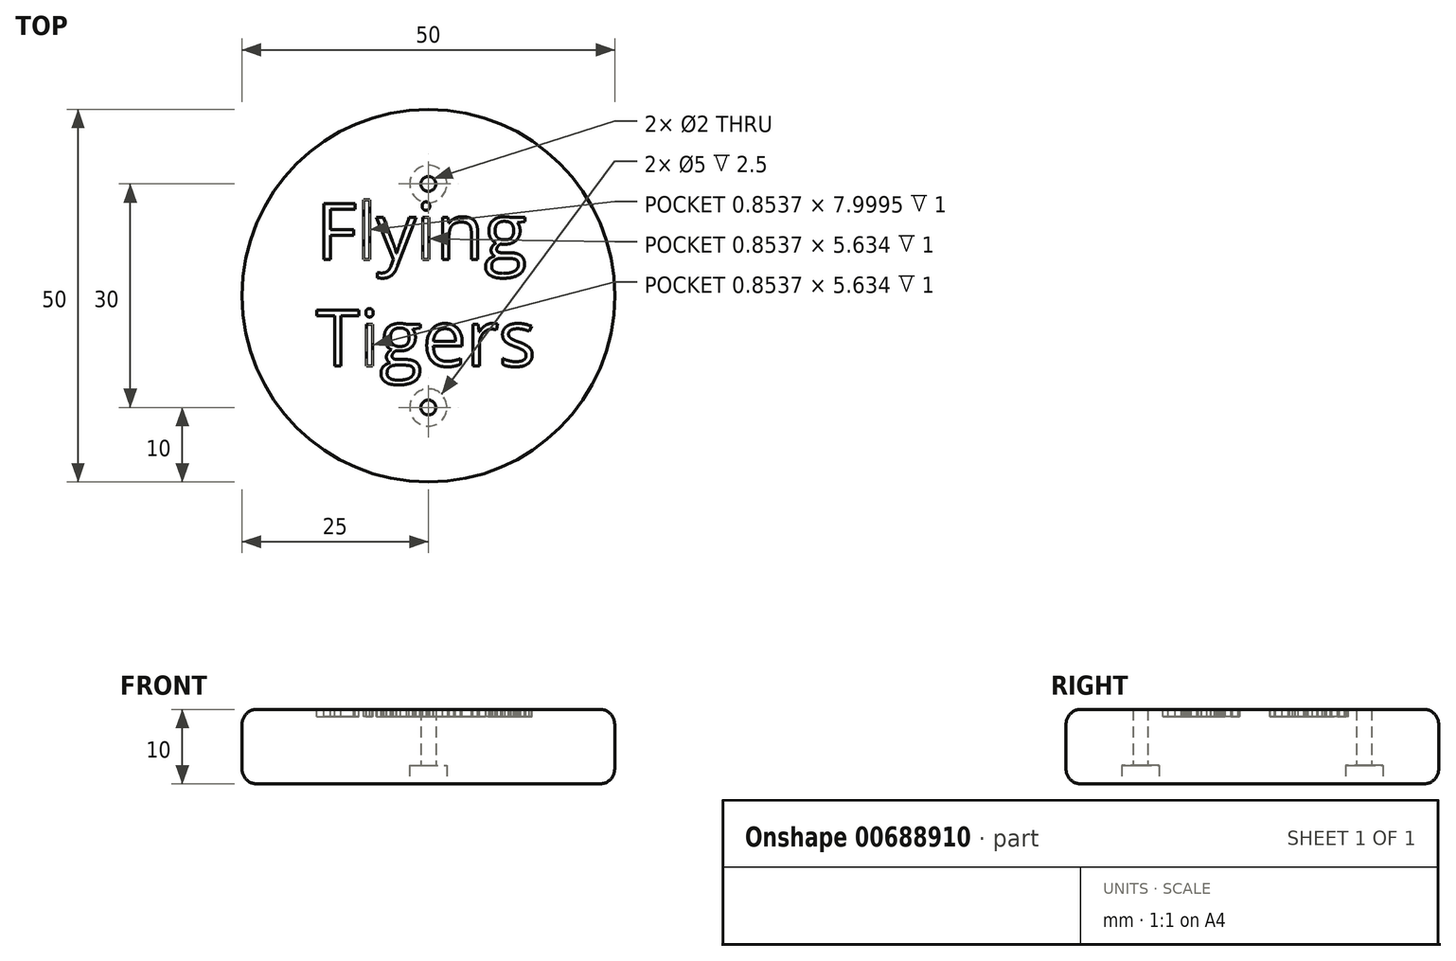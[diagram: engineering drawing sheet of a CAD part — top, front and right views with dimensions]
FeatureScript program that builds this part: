
annotation { "Feature Type Name" : "Feature", "Feature Type Description" : "" }
export const myFeature = defineFeature(function(context is Context, id is Id, definition is map)
    precondition{}
    {
        {
            var Q0;
            Q0=qCreatedBy(makeId("Top.planeOp"),FACE);
            var sketch = newSketch(context, id + "F0", { "sketchPlane" : qUnion([Q0])});
            skCircle(sketch, "E0", {"center": v(0, 0) * mm, "radius": 25 * mm});
            skSolve(sketch);
        }
        {
            var Q0;
            Q0=qSketchRegion(id+"F0",true);
            extrude(context, id + "F1", {"entities" : qUnion([Q0]), "depth" : 10 * mm});
        }
        {
            var Q0;
            Q0=makeQuery(id+"F1.opExtrude","CAP_FACE",FACE,{"disambiguationData":[OSD([sQuery(id+"F0.wireOp",EDGE,"E0")])],"isStart":false});
            var sketch = newSketch(context, id + "F2", { "sketchPlane" : qUnion([Q0])});
            skText(sketch, "E1", { "text": "GO DOGS", "fontName": "OpenSans-Bold.ttf"});
            const initialGuessF2  = {"E1": [-0.02326, -0.00364, 1, 0, 0.007]};
            skSetInitialGuess(sketch, initialGuessF2);
            skSolve(sketch);
        }
        {
            var Q0;
            Q0=qSketchRegion(id+"F2",true);
            extrude(context, id + "F3", {"entities" : qUnion([Q0]), "operationType" : NewBodyOperationType.REMOVE, "oppositeDirection" : true, "depth" : 1 * mm});
        }
        {
            var Q0;
            Q0=makeQuery(id+"F1.opExtrude","CAP_EDGE",EDGE,{"disambiguationData":[OSD([sQuery(id+"F0.wireOp",EDGE,"E0")])],"isStart":false});
            var Q1;
            Q1=makeQuery(id+"F1.opExtrude","CAP_EDGE",EDGE,{"disambiguationData":[OSD([sQuery(id+"F0.wireOp",EDGE,"E0")])],"isStart":true});
            fillet(context, id + "F4", {"entities" : qUnion([Q0, Q1]), "radius" : 2 * mm, "tangentPropagation" : true, "allowEdgeOverflow" : false});
        }
        {
            var Q0;
            Q0=makeQuery(id+"F1.opExtrude","CAP_FACE",FACE,{"disambiguationData":[OSD([sQuery(id+"F0.wireOp",EDGE,"E0")])],"isStart":true});
            var sketch = newSketch(context, id + "F5", { "sketchPlane" : qUnion([Q0])});
            skPoint(sketch, "E2", {"position": v(0, 15) * mm});
            skPoint(sketch, "E3", {"position": v(0, -15) * mm});
            skSolve(sketch);
        }
        {
            var Q0;
            Q0=sQuery(id+"F5.wireOp",VERTEX,"E2");
            var Q1;
            Q1=sQuery(id+"F5.wireOp",VERTEX,"E3");
            var Q2;
            Q2=makeQuery(id+"F1.opExtrude","SWEPT_BODY",BODY,{"disambiguationData":[OSD([sQuery(id+"F0.wireOp",EDGE,"E0")])]});
            hole(context, id + "F6", {"style" : HoleStyle.C_BORE, "endStyle" : HoleEndStyle.THROUGH, "holeDiameter" : 2 * mm, "cBoreDiameter" : 5 * mm, "cBoreDepth" : 2.5 * mm, "startFromSketch" : true, "locations" : qUnion([Q0, Q1]), "scope" : qUnion([Q2]), "isTappedThrough" : true});
        }
        {
            var Q0;
            Q0=makeQuery(id+"F3.boolean.opBoolean","COPY",FACE,{"derivedFrom":makeQuery(id+"F3.opExtrude","CAP_FACE",FACE,{"disambiguationData":[OSD([sQuery(id+"F2.wireOp",EDGE,"E1.sketch_text.stroke-0"),sQuery(id+"F2.wireOp",EDGE,"E1.sketch_text.stroke-1"),sQuery(id+"F2.wireOp",EDGE,"E1.sketch_text.stroke-2"),sQuery(id+"F2.wireOp",EDGE,"E1.sketch_text.stroke-3"),sQuery(id+"F2.wireOp",EDGE,"E1.sketch_text.stroke-4"),sQuery(id+"F2.wireOp",EDGE,"E1.sketch_text.stroke-5"),sQuery(id+"F2.wireOp",EDGE,"E1.sketch_text.stroke-6"),sQuery(id+"F2.wireOp",EDGE,"E1.sketch_text.stroke-7"),sQuery(id+"F2.wireOp",EDGE,"E1.sketch_text.stroke-8"),sQuery(id+"F2.wireOp",EDGE,"E1.sketch_text.stroke-9"),sQuery(id+"F2.wireOp",EDGE,"E1.sketch_text.stroke-10"),sQuery(id+"F2.wireOp",EDGE,"E1.sketch_text.stroke-11"),sQuery(id+"F2.wireOp",EDGE,"E1.sketch_text.stroke-12"),sQuery(id+"F2.wireOp",EDGE,"E1.sketch_text.stroke-13"),sQuery(id+"F2.wireOp",EDGE,"E1.sketch_text.stroke-14"),sQuery(id+"F2.wireOp",EDGE,"E1.sketch_text.stroke-15"),sQuery(id+"F2.wireOp",EDGE,"E1.sketch_text.stroke-16"),sQuery(id+"F2.wireOp",EDGE,"E1.sketch_text.stroke-17"),sQuery(id+"F2.wireOp",EDGE,"E1.sketch_text.stroke-18")])],"isStart":false})});
            extrude(context, id + "F7", {"entities" : qUnion([Q0]), "operationType" : NewBodyOperationType.ADD, "depth" : 1 * mm, "offsetDistance" : 25 * mm});
        }
        {
            var Q0;
            Q0=makeQuery(id+"F3.boolean.opBoolean","COPY",FACE,{"derivedFrom":makeQuery(id+"F3.opExtrude","CAP_FACE",FACE,{"disambiguationData":[OSD([sQuery(id+"F2.wireOp",EDGE,"E1.sketch_text.stroke-19"),sQuery(id+"F2.wireOp",EDGE,"E1.sketch_text.stroke-20"),sQuery(id+"F2.wireOp",EDGE,"E1.sketch_text.stroke-21"),sQuery(id+"F2.wireOp",EDGE,"E1.sketch_text.stroke-22"),sQuery(id+"F2.wireOp",EDGE,"E1.sketch_text.stroke-23"),sQuery(id+"F2.wireOp",EDGE,"E1.sketch_text.stroke-24"),sQuery(id+"F2.wireOp",EDGE,"E1.sketch_text.stroke-25"),sQuery(id+"F2.wireOp",EDGE,"E1.sketch_text.stroke-26"),sQuery(id+"F2.wireOp",EDGE,"E1.sketch_text.stroke-27"),sQuery(id+"F2.wireOp",EDGE,"E1.sketch_text.stroke-28"),sQuery(id+"F2.wireOp",EDGE,"E1.sketch_text.stroke-29"),sQuery(id+"F2.wireOp",EDGE,"E1.sketch_text.stroke-30"),sQuery(id+"F2.wireOp",EDGE,"E1.sketch_text.stroke-31"),sQuery(id+"F2.wireOp",EDGE,"E1.sketch_text.stroke-32")])],"isStart":false})});
            extrude(context, id + "F8", {"entities" : qUnion([Q0]), "operationType" : NewBodyOperationType.ADD, "depth" : 1 * mm, "offsetDistance" : 25 * mm});
        }
        {
            var Q0;
            Q0=makeQuery(id+"F3.boolean.opBoolean","COPY",FACE,{"derivedFrom":makeQuery(id+"F3.opExtrude","CAP_FACE",FACE,{"disambiguationData":[OSD([sQuery(id+"F2.wireOp",EDGE,"E1.sketch_text.stroke-33"),sQuery(id+"F2.wireOp",EDGE,"E1.sketch_text.stroke-34"),sQuery(id+"F2.wireOp",EDGE,"E1.sketch_text.stroke-35"),sQuery(id+"F2.wireOp",EDGE,"E1.sketch_text.stroke-36"),sQuery(id+"F2.wireOp",EDGE,"E1.sketch_text.stroke-37"),sQuery(id+"F2.wireOp",EDGE,"E1.sketch_text.stroke-38"),sQuery(id+"F2.wireOp",EDGE,"E1.sketch_text.stroke-39"),sQuery(id+"F2.wireOp",EDGE,"E1.sketch_text.stroke-40"),sQuery(id+"F2.wireOp",EDGE,"E1.sketch_text.stroke-41"),sQuery(id+"F2.wireOp",EDGE,"E1.sketch_text.stroke-42"),sQuery(id+"F2.wireOp",EDGE,"E1.sketch_text.stroke-43"),sQuery(id+"F2.wireOp",EDGE,"E1.sketch_text.stroke-44")])],"isStart":false})});
            extrude(context, id + "F9", {"entities" : qUnion([Q0]), "operationType" : NewBodyOperationType.ADD, "depth" : 1 * mm, "offsetDistance" : 25 * mm});
        }
        {
            var Q0;
            Q0=makeQuery(id+"F3.boolean.opBoolean","COPY",FACE,{"derivedFrom":makeQuery(id+"F3.opExtrude","CAP_FACE",FACE,{"disambiguationData":[OSD([sQuery(id+"F2.wireOp",EDGE,"E1.sketch_text.stroke-59"),sQuery(id+"F2.wireOp",EDGE,"E1.sketch_text.stroke-60"),sQuery(id+"F2.wireOp",EDGE,"E1.sketch_text.stroke-61"),sQuery(id+"F2.wireOp",EDGE,"E1.sketch_text.stroke-62"),sQuery(id+"F2.wireOp",EDGE,"E1.sketch_text.stroke-63"),sQuery(id+"F2.wireOp",EDGE,"E1.sketch_text.stroke-64"),sQuery(id+"F2.wireOp",EDGE,"E1.sketch_text.stroke-65"),sQuery(id+"F2.wireOp",EDGE,"E1.sketch_text.stroke-66"),sQuery(id+"F2.wireOp",EDGE,"E1.sketch_text.stroke-67"),sQuery(id+"F2.wireOp",EDGE,"E1.sketch_text.stroke-68"),sQuery(id+"F2.wireOp",EDGE,"E1.sketch_text.stroke-69"),sQuery(id+"F2.wireOp",EDGE,"E1.sketch_text.stroke-70"),sQuery(id+"F2.wireOp",EDGE,"E1.sketch_text.stroke-71"),sQuery(id+"F2.wireOp",EDGE,"E1.sketch_text.stroke-72"),sQuery(id+"F2.wireOp",EDGE,"E1.sketch_text.stroke-73"),sQuery(id+"F2.wireOp",EDGE,"E1.sketch_text.stroke-74"),sQuery(id+"F2.wireOp",EDGE,"E1.sketch_text.stroke-75"),sQuery(id+"F2.wireOp",EDGE,"E1.sketch_text.stroke-76"),sQuery(id+"F2.wireOp",EDGE,"E1.sketch_text.stroke-77")])],"isStart":false})});
            var Q1;
            Q1=makeQuery(id+"F3.boolean.opBoolean","COPY",FACE,{"derivedFrom":makeQuery(id+"F3.opExtrude","CAP_FACE",FACE,{"disambiguationData":[OSD([sQuery(id+"F2.wireOp",EDGE,"E1.sketch_text.stroke-45"),sQuery(id+"F2.wireOp",EDGE,"E1.sketch_text.stroke-46"),sQuery(id+"F2.wireOp",EDGE,"E1.sketch_text.stroke-47"),sQuery(id+"F2.wireOp",EDGE,"E1.sketch_text.stroke-48"),sQuery(id+"F2.wireOp",EDGE,"E1.sketch_text.stroke-49"),sQuery(id+"F2.wireOp",EDGE,"E1.sketch_text.stroke-50"),sQuery(id+"F2.wireOp",EDGE,"E1.sketch_text.stroke-51"),sQuery(id+"F2.wireOp",EDGE,"E1.sketch_text.stroke-52"),sQuery(id+"F2.wireOp",EDGE,"E1.sketch_text.stroke-53"),sQuery(id+"F2.wireOp",EDGE,"E1.sketch_text.stroke-54"),sQuery(id+"F2.wireOp",EDGE,"E1.sketch_text.stroke-55"),sQuery(id+"F2.wireOp",EDGE,"E1.sketch_text.stroke-56"),sQuery(id+"F2.wireOp",EDGE,"E1.sketch_text.stroke-57"),sQuery(id+"F2.wireOp",EDGE,"E1.sketch_text.stroke-58")])],"isStart":false})});
            var Q2;
            Q2=makeQuery(id+"F3.boolean.opBoolean","COPY",FACE,{"derivedFrom":makeQuery(id+"F3.opExtrude","CAP_FACE",FACE,{"disambiguationData":[OSD([sQuery(id+"F2.wireOp",EDGE,"E1.sketch_text.stroke-78"),sQuery(id+"F2.wireOp",EDGE,"E1.sketch_text.stroke-79"),sQuery(id+"F2.wireOp",EDGE,"E1.sketch_text.stroke-80"),sQuery(id+"F2.wireOp",EDGE,"E1.sketch_text.stroke-81"),sQuery(id+"F2.wireOp",EDGE,"E1.sketch_text.stroke-82"),sQuery(id+"F2.wireOp",EDGE,"E1.sketch_text.stroke-83"),sQuery(id+"F2.wireOp",EDGE,"E1.sketch_text.stroke-84"),sQuery(id+"F2.wireOp",EDGE,"E1.sketch_text.stroke-85"),sQuery(id+"F2.wireOp",EDGE,"E1.sketch_text.stroke-86"),sQuery(id+"F2.wireOp",EDGE,"E1.sketch_text.stroke-87"),sQuery(id+"F2.wireOp",EDGE,"E1.sketch_text.stroke-88"),sQuery(id+"F2.wireOp",EDGE,"E1.sketch_text.stroke-89"),sQuery(id+"F2.wireOp",EDGE,"E1.sketch_text.stroke-90"),sQuery(id+"F2.wireOp",EDGE,"E1.sketch_text.stroke-91"),sQuery(id+"F2.wireOp",EDGE,"E1.sketch_text.stroke-92"),sQuery(id+"F2.wireOp",EDGE,"E1.sketch_text.stroke-93"),sQuery(id+"F2.wireOp",EDGE,"E1.sketch_text.stroke-94"),sQuery(id+"F2.wireOp",EDGE,"E1.sketch_text.stroke-95"),sQuery(id+"F2.wireOp",EDGE,"E1.sketch_text.stroke-96"),sQuery(id+"F2.wireOp",EDGE,"E1.sketch_text.stroke-97"),sQuery(id+"F2.wireOp",EDGE,"E1.sketch_text.stroke-98"),sQuery(id+"F2.wireOp",EDGE,"E1.sketch_text.stroke-99"),sQuery(id+"F2.wireOp",EDGE,"E1.sketch_text.stroke-100"),sQuery(id+"F2.wireOp",EDGE,"E1.sketch_text.stroke-101"),sQuery(id+"F2.wireOp",EDGE,"E1.sketch_text.stroke-102"),sQuery(id+"F2.wireOp",EDGE,"E1.sketch_text.stroke-103"),sQuery(id+"F2.wireOp",EDGE,"E1.sketch_text.stroke-104"),sQuery(id+"F2.wireOp",EDGE,"E1.sketch_text.stroke-105")])],"isStart":false})});
            extrude(context, id + "F10", {"entities" : qUnion([Q0, Q1, Q2]), "operationType" : NewBodyOperationType.ADD, "depth" : 1 * mm, "offsetDistance" : 25 * mm});
        }
        {
            var Q0;
            {var subQ0=sQuery(id+"F2.wireOp",EDGE,"E1.sketch_text.stroke-105");var subQ1=sQuery(id+"F2.wireOp",EDGE,"E1.sketch_text.stroke-104");var subQ2=sQuery(id+"F2.wireOp",EDGE,"E1.sketch_text.stroke-103");var subQ3=sQuery(id+"F2.wireOp",EDGE,"E1.sketch_text.stroke-102");var subQ4=sQuery(id+"F2.wireOp",EDGE,"E1.sketch_text.stroke-101");var subQ5=sQuery(id+"F2.wireOp",EDGE,"E1.sketch_text.stroke-100");var subQ6=sQuery(id+"F2.wireOp",EDGE,"E1.sketch_text.stroke-99");var subQ7=sQuery(id+"F2.wireOp",EDGE,"E1.sketch_text.stroke-98");var subQ8=sQuery(id+"F2.wireOp",EDGE,"E1.sketch_text.stroke-97");var subQ9=sQuery(id+"F2.wireOp",EDGE,"E1.sketch_text.stroke-96");var subQ10=sQuery(id+"F2.wireOp",EDGE,"E1.sketch_text.stroke-95");var subQ11=sQuery(id+"F2.wireOp",EDGE,"E1.sketch_text.stroke-94");var subQ12=sQuery(id+"F2.wireOp",EDGE,"E1.sketch_text.stroke-93");var subQ13=sQuery(id+"F2.wireOp",EDGE,"E1.sketch_text.stroke-92");var subQ14=sQuery(id+"F2.wireOp",EDGE,"E1.sketch_text.stroke-91");var subQ15=sQuery(id+"F2.wireOp",EDGE,"E1.sketch_text.stroke-90");var subQ16=sQuery(id+"F2.wireOp",EDGE,"E1.sketch_text.stroke-89");var subQ17=sQuery(id+"F2.wireOp",EDGE,"E1.sketch_text.stroke-88");var subQ18=sQuery(id+"F2.wireOp",EDGE,"E1.sketch_text.stroke-87");var subQ19=sQuery(id+"F2.wireOp",EDGE,"E1.sketch_text.stroke-86");var subQ20=sQuery(id+"F2.wireOp",EDGE,"E1.sketch_text.stroke-85");var subQ21=sQuery(id+"F2.wireOp",EDGE,"E1.sketch_text.stroke-84");var subQ22=sQuery(id+"F2.wireOp",EDGE,"E1.sketch_text.stroke-83");var subQ23=sQuery(id+"F2.wireOp",EDGE,"E1.sketch_text.stroke-82");var subQ24=sQuery(id+"F2.wireOp",EDGE,"E1.sketch_text.stroke-81");var subQ25=sQuery(id+"F2.wireOp",EDGE,"E1.sketch_text.stroke-80");var subQ26=sQuery(id+"F2.wireOp",EDGE,"E1.sketch_text.stroke-79");var subQ27=sQuery(id+"F2.wireOp",EDGE,"E1.sketch_text.stroke-78");var subQ28=sQuery(id+"F2.wireOp",EDGE,"E1.sketch_text.stroke-77");var subQ29=sQuery(id+"F2.wireOp",EDGE,"E1.sketch_text.stroke-76");var subQ30=sQuery(id+"F2.wireOp",EDGE,"E1.sketch_text.stroke-75");var subQ31=sQuery(id+"F2.wireOp",EDGE,"E1.sketch_text.stroke-74");var subQ32=sQuery(id+"F2.wireOp",EDGE,"E1.sketch_text.stroke-73");var subQ33=sQuery(id+"F2.wireOp",EDGE,"E1.sketch_text.stroke-72");var subQ34=sQuery(id+"F2.wireOp",EDGE,"E1.sketch_text.stroke-71");var subQ35=sQuery(id+"F2.wireOp",EDGE,"E1.sketch_text.stroke-70");var subQ36=sQuery(id+"F2.wireOp",EDGE,"E1.sketch_text.stroke-69");var subQ37=sQuery(id+"F2.wireOp",EDGE,"E1.sketch_text.stroke-68");var subQ38=sQuery(id+"F2.wireOp",EDGE,"E1.sketch_text.stroke-67");var subQ39=sQuery(id+"F2.wireOp",EDGE,"E1.sketch_text.stroke-66");var subQ40=sQuery(id+"F2.wireOp",EDGE,"E1.sketch_text.stroke-65");var subQ41=sQuery(id+"F2.wireOp",EDGE,"E1.sketch_text.stroke-64");var subQ42=sQuery(id+"F2.wireOp",EDGE,"E1.sketch_text.stroke-63");var subQ43=sQuery(id+"F2.wireOp",EDGE,"E1.sketch_text.stroke-62");var subQ44=sQuery(id+"F2.wireOp",EDGE,"E1.sketch_text.stroke-61");var subQ45=sQuery(id+"F2.wireOp",EDGE,"E1.sketch_text.stroke-60");var subQ46=sQuery(id+"F2.wireOp",EDGE,"E1.sketch_text.stroke-59");var subQ47=sQuery(id+"F2.wireOp",EDGE,"E1.sketch_text.stroke-58");var subQ48=sQuery(id+"F2.wireOp",EDGE,"E1.sketch_text.stroke-57");var subQ49=sQuery(id+"F2.wireOp",EDGE,"E1.sketch_text.stroke-56");var subQ50=sQuery(id+"F2.wireOp",EDGE,"E1.sketch_text.stroke-55");var subQ51=sQuery(id+"F2.wireOp",EDGE,"E1.sketch_text.stroke-54");var subQ52=sQuery(id+"F2.wireOp",EDGE,"E1.sketch_text.stroke-53");var subQ53=sQuery(id+"F2.wireOp",EDGE,"E1.sketch_text.stroke-52");var subQ54=sQuery(id+"F2.wireOp",EDGE,"E1.sketch_text.stroke-51");var subQ55=sQuery(id+"F2.wireOp",EDGE,"E1.sketch_text.stroke-50");var subQ56=sQuery(id+"F2.wireOp",EDGE,"E1.sketch_text.stroke-49");var subQ57=sQuery(id+"F2.wireOp",EDGE,"E1.sketch_text.stroke-48");var subQ58=sQuery(id+"F2.wireOp",EDGE,"E1.sketch_text.stroke-47");var subQ59=sQuery(id+"F2.wireOp",EDGE,"E1.sketch_text.stroke-46");var subQ60=sQuery(id+"F2.wireOp",EDGE,"E1.sketch_text.stroke-45");var subQ61=sQuery(id+"F2.wireOp",EDGE,"E1.sketch_text.stroke-44");var subQ62=sQuery(id+"F2.wireOp",EDGE,"E1.sketch_text.stroke-43");var subQ63=sQuery(id+"F2.wireOp",EDGE,"E1.sketch_text.stroke-42");var subQ64=sQuery(id+"F2.wireOp",EDGE,"E1.sketch_text.stroke-41");var subQ65=sQuery(id+"F2.wireOp",EDGE,"E1.sketch_text.stroke-40");var subQ66=sQuery(id+"F2.wireOp",EDGE,"E1.sketch_text.stroke-39");var subQ67=sQuery(id+"F2.wireOp",EDGE,"E1.sketch_text.stroke-38");var subQ68=sQuery(id+"F2.wireOp",EDGE,"E1.sketch_text.stroke-37");var subQ69=sQuery(id+"F2.wireOp",EDGE,"E1.sketch_text.stroke-36");var subQ70=sQuery(id+"F2.wireOp",EDGE,"E1.sketch_text.stroke-35");var subQ71=sQuery(id+"F2.wireOp",EDGE,"E1.sketch_text.stroke-34");var subQ72=sQuery(id+"F2.wireOp",EDGE,"E1.sketch_text.stroke-33");var subQ73=sQuery(id+"F2.wireOp",EDGE,"E1.sketch_text.stroke-32");var subQ74=sQuery(id+"F2.wireOp",EDGE,"E1.sketch_text.stroke-31");var subQ75=sQuery(id+"F2.wireOp",EDGE,"E1.sketch_text.stroke-30");var subQ76=sQuery(id+"F2.wireOp",EDGE,"E1.sketch_text.stroke-29");var subQ77=sQuery(id+"F2.wireOp",EDGE,"E1.sketch_text.stroke-28");var subQ78=sQuery(id+"F2.wireOp",EDGE,"E1.sketch_text.stroke-27");var subQ79=sQuery(id+"F2.wireOp",EDGE,"E1.sketch_text.stroke-26");var subQ80=sQuery(id+"F2.wireOp",EDGE,"E1.sketch_text.stroke-25");var subQ81=sQuery(id+"F2.wireOp",EDGE,"E1.sketch_text.stroke-24");var subQ82=sQuery(id+"F2.wireOp",EDGE,"E1.sketch_text.stroke-23");var subQ83=sQuery(id+"F2.wireOp",EDGE,"E1.sketch_text.stroke-22");var subQ84=sQuery(id+"F2.wireOp",EDGE,"E1.sketch_text.stroke-21");var subQ85=sQuery(id+"F2.wireOp",EDGE,"E1.sketch_text.stroke-20");var subQ86=sQuery(id+"F2.wireOp",EDGE,"E1.sketch_text.stroke-19");var subQ87=sQuery(id+"F2.wireOp",EDGE,"E1.sketch_text.stroke-18");var subQ88=sQuery(id+"F2.wireOp",EDGE,"E1.sketch_text.stroke-17");var subQ89=sQuery(id+"F2.wireOp",EDGE,"E1.sketch_text.stroke-16");var subQ90=sQuery(id+"F2.wireOp",EDGE,"E1.sketch_text.stroke-15");var subQ91=sQuery(id+"F2.wireOp",EDGE,"E1.sketch_text.stroke-14");var subQ92=sQuery(id+"F2.wireOp",EDGE,"E1.sketch_text.stroke-13");var subQ93=sQuery(id+"F2.wireOp",EDGE,"E1.sketch_text.stroke-12");var subQ94=sQuery(id+"F2.wireOp",EDGE,"E1.sketch_text.stroke-11");var subQ95=sQuery(id+"F2.wireOp",EDGE,"E1.sketch_text.stroke-10");var subQ96=sQuery(id+"F2.wireOp",EDGE,"E1.sketch_text.stroke-9");var subQ97=sQuery(id+"F2.wireOp",EDGE,"E1.sketch_text.stroke-8");var subQ98=sQuery(id+"F2.wireOp",EDGE,"E1.sketch_text.stroke-7");var subQ99=sQuery(id+"F2.wireOp",EDGE,"E1.sketch_text.stroke-6");var subQ100=sQuery(id+"F2.wireOp",EDGE,"E1.sketch_text.stroke-5");var subQ101=sQuery(id+"F2.wireOp",EDGE,"E1.sketch_text.stroke-4");var subQ102=sQuery(id+"F2.wireOp",EDGE,"E1.sketch_text.stroke-3");var subQ103=sQuery(id+"F2.wireOp",EDGE,"E1.sketch_text.stroke-2");var subQ104=sQuery(id+"F2.wireOp",EDGE,"E1.sketch_text.stroke-1");var subQ105=sQuery(id+"F2.wireOp",EDGE,"E1.sketch_text.stroke-0");var subQ106=sQuery(id+"F0.wireOp",EDGE,"E0");var subQ107=makeQuery(id+"F1.opExtrude","CAP_FACE",FACE,{"disambiguationData":[OSD([subQ106])],"isStart":false});Q0=makeQuery(id+"F10.boolean.opBoolean","MERGE",FACE,{"derivedFrom":[makeQuery(id+"F3.boolean.opBoolean","SPLIT",FACE,{"disambiguationData":[TD([makeQuery(id+"F3.opExtrude","SWEPT_FACE",FACE,{"disambiguationData":[OSD([subQ52])]})])],"derivedFrom":subQ107}),makeQuery(id+"F9.boolean.opBoolean","MERGE",FACE,{"derivedFrom":[makeQuery(id+"F3.boolean.opBoolean","SPLIT",FACE,{"disambiguationData":[TD([makeQuery(id+"F3.opExtrude","SWEPT_FACE",FACE,{"disambiguationData":[OSD([subQ65])]})])],"derivedFrom":subQ107}),makeQuery(id+"F8.boolean.opBoolean","MERGE",FACE,{"derivedFrom":[makeQuery(id+"F3.boolean.opBoolean","SPLIT",FACE,{"disambiguationData":[TD([makeQuery(id+"F3.opExtrude","SWEPT_FACE",FACE,{"disambiguationData":[OSD([subQ78])]})])],"derivedFrom":subQ107}),makeQuery(id+"F7.boolean.opBoolean","MERGE",FACE,{"derivedFrom":[makeQuery(id+"F3.boolean.opBoolean","SPLIT",FACE,{"disambiguationData":[TD([makeQuery(id+"F1.opExtrude","SWEPT_FACE",FACE,{"disambiguationData":[OSD([subQ106])]})])],"derivedFrom":subQ107}),makeQuery(id+"F7.opExtrude","CAP_FACE",FACE,{"disambiguationData":[OSD([subQ105,subQ104,subQ103,subQ102,subQ101,subQ100,subQ99,subQ98,subQ97,subQ96,subQ95,subQ94,subQ93,subQ92,subQ91,subQ90,subQ89,subQ88,subQ87])],"isStart":false})]}),makeQuery(id+"F8.opExtrude","CAP_FACE",FACE,{"disambiguationData":[OSD([subQ86,subQ85,subQ84,subQ83,subQ82,subQ81,subQ80,subQ79,subQ78,subQ77,subQ76,subQ75,subQ74,subQ73])],"isStart":false})]}),makeQuery(id+"F9.opExtrude","CAP_FACE",FACE,{"disambiguationData":[OSD([subQ72,subQ71,subQ70,subQ69,subQ68,subQ67,subQ66,subQ65,subQ64,subQ63,subQ62,subQ61])],"isStart":false})]}),makeQuery(id+"F10.opExtrude","CAP_FACE",FACE,{"disambiguationData":[OSD([subQ60,subQ59,subQ58,subQ57,subQ56,subQ55,subQ54,subQ53,subQ52,subQ51,subQ50,subQ49,subQ48,subQ47])],"isStart":false}),makeQuery(id+"F10.opExtrude","CAP_FACE",FACE,{"disambiguationData":[OSD([subQ46,subQ45,subQ44,subQ43,subQ42,subQ41,subQ40,subQ39,subQ38,subQ37,subQ36,subQ35,subQ34,subQ33,subQ32,subQ31,subQ30,subQ29,subQ28])],"isStart":false}),makeQuery(id+"F10.opExtrude","CAP_FACE",FACE,{"disambiguationData":[OSD([subQ27,subQ26,subQ25,subQ24,subQ23,subQ22,subQ21,subQ20,subQ19,subQ18,subQ17,subQ16,subQ15,subQ14,subQ13,subQ12,subQ11,subQ10,subQ9,subQ8,subQ7,subQ6,subQ5,subQ4,subQ3,subQ2,subQ1,subQ0])],"isStart":false})]});}
            var sketch = newSketch(context, id + "F11", { "sketchPlane" : qUnion([Q0])});
            skText(sketch, "E4", { "text": "Flying\nTigers", "fontName": "OpenSans-Regular.ttf"});
            const initialGuessF11  = {"E4": [-0.01506, 0.00487, 1, 0, 0.00758]};
            skSetInitialGuess(sketch, initialGuessF11);
            skSolve(sketch);
        }
        {
            var Q0;
            Q0 = qSketchRegion(id + "F11", true);
            extrude(context, id + "F12", {"entities" : qUnion([Q0]), "operationType" : NewBodyOperationType.REMOVE, "oppositeDirection" : true, "depth" : 1 * mm, "offsetDistance" : 25 * mm});
        }
    });
